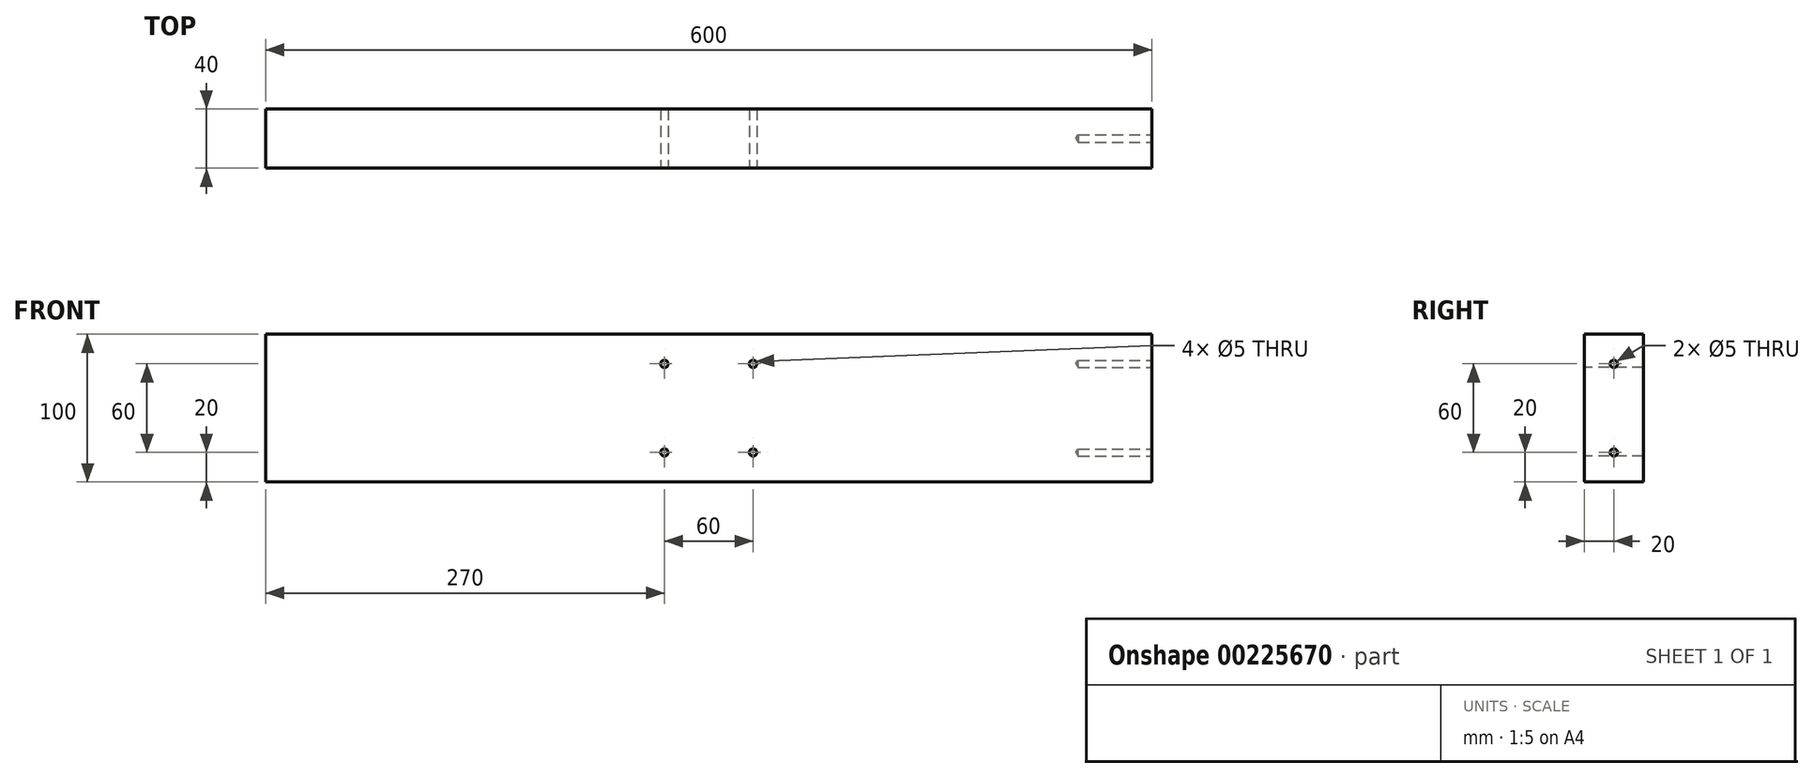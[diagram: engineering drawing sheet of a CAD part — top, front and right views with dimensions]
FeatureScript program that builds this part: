
annotation { "Feature Type Name" : "Feature", "Feature Type Description" : "" }
export const myFeature = defineFeature(function(context is Context, id is Id, definition is map)
    precondition{}
    {
        {
            var Q0;
            Q0=qCreatedBy(makeId("Front.planeOp"),FACE);
            var sketch = newSketch(context, id + "F0", { "sketchPlane" : qUnion([Q0])});
            skLineSegment(sketch, "E0.bottom", {"start": v(-300, 50) * mm, "end": v(300, 50) * mm});
            skLineSegment(sketch, "E0.top", {"start": v(-300, -50) * mm, "end": v(300, -50) * mm});
            skLineSegment(sketch, "E0.left", {"start": v(-300, 50) * mm, "end": v(-300, -50) * mm});
            skLineSegment(sketch, "E0.right", {"start": v(300, 50) * mm, "end": v(300, -50) * mm});
            skLineSegment(sketch, "E1", {"start": v(0, 50) * mm, "end": v(0, -50) * mm, "construction": true});
            skLineSegment(sketch, "E2", {"start": v(-300, 0) * mm, "end": v(300, 0) * mm, "construction": true});
            skSolve(sketch);
        }
        {
            var Q0;
            Q0=makeQuery(id+"F0.imprint","IMPRINT",FACE,{"disambiguationData":[TD([[makeQuery(id+"F0.imprint","IMPRINT",EDGE,{"derivedFrom":sQuery(id+"F0.wireOp",EDGE,"E0.bottom")}),-1.0]])]});
            extrude(context, id + "F1", {"entities" : qUnion([Q0]), "endBound" : BoundingType.SYMMETRIC, "depth" : 40 * mm});
        }
        {
            var Q0;
            Q0=makeQuery(id+"F1.opExtrude","CAP_FACE",FACE,{"disambiguationData":[OSD([sQuery(id+"F0.wireOp",EDGE,"E0.bottom"),sQuery(id+"F0.wireOp",EDGE,"E0.top"),sQuery(id+"F0.wireOp",EDGE,"E0.left"),sQuery(id+"F0.wireOp",EDGE,"E0.right")])],"isStart":false});
            var sketch = newSketch(context, id + "F2", { "sketchPlane" : qUnion([Q0])});
            skLineSegment(sketch, "E3", {"start": v(50, 50) * mm, "end": v(50, -50) * mm, "construction": true});
            skPoint(sketch, "E4", {"position": v(30, 30) * mm});
            skPoint(sketch, "E5", {"position": v(30, -30) * mm});
            skPoint(sketch, "E6", {"position": v(-30, 30) * mm});
            skPoint(sketch, "E7", {"position": v(-30, -30) * mm});
            skSolve(sketch);
        }
        {
            var Q0;
            Q0=sQuery(id+"F2.wireOp",VERTEX,"d4a535e9-99f7-48f2-8113-ce6ab7c4a757");
            var Q1;
            Q1=sQuery(id+"F2.wireOp",VERTEX,"bcf1949b-d54f-4d90-9dce-a7bc10d12a4c");
            var Q2;
            Q2=sQuery(id+"F2.wireOp",VERTEX,"2863efec-cea9-4b0d-8fdf-9ae05410bcc6");
            var Q3;
            Q3=sQuery(id+"F2.wireOp",VERTEX,"1f114518-a88e-412f-a738-b101c2e852a8");
            var Q4;
            Q4=sQuery(id+"F2.wireOp",VERTEX,"E6");
            var Q5;
            Q5=sQuery(id+"F2.wireOp",VERTEX,"E4");
            var Q6;
            Q6=sQuery(id+"F2.wireOp",VERTEX,"E7");
            var Q7;
            Q7=sQuery(id+"F2.wireOp",VERTEX,"E5");
            var Q8;
            Q8=sQuery(id+"F2.wireOp",VERTEX,"6d67d9a1-f94c-460c-9f3e-7900fbfed6ee");
            var Q9;
            Q9=sQuery(id+"F2.wireOp",VERTEX,"3c76ddc9-934c-45bd-b5f3-5c4f99041eee");
            var Q10;
            Q10=sQuery(id+"F2.wireOp",VERTEX,"663380e0-082c-4e9e-85f6-5e861101b0f0");
            var Q11;
            Q11=sQuery(id+"F2.wireOp",VERTEX,"c1c2a8b6-fc07-4b36-872f-67ce65da0087");
            var Q12;
            Q12=makeQuery(id+"F1.opExtrude","SWEPT_BODY",BODY,{"disambiguationData":[OSD([sQuery(id+"F0.wireOp",EDGE,"E0.bottom"),sQuery(id+"F0.wireOp",EDGE,"E0.top"),sQuery(id+"F0.wireOp",EDGE,"E0.left"),sQuery(id+"F0.wireOp",EDGE,"E0.right")])]});
            hole(context, id + "F3", {"style" : HoleStyle.SIMPLE, "endStyle" : HoleEndStyle.THROUGH, "holeDiameter" : 5 * mm, "locations" : qUnion([Q0, Q1, Q2, Q3, Q4, Q5, Q6, Q7, Q8, Q9, Q10, Q11]), "scope" : qUnion([Q12]), "isTappedThrough" : true});
        }
        {
            var Q0;
            Q0=makeQuery(id+"F1.opExtrude","SWEPT_FACE",FACE,{"disambiguationData":[OSD([sQuery(id+"F0.wireOp",EDGE,"E0.right")])]});
            var sketch = newSketch(context, id + "F4", { "sketchPlane" : qUnion([Q0])});
            skPoint(sketch, "E8", {"position": v(0, 30) * mm});
            skPoint(sketch, "E9", {"position": v(0, -30) * mm});
            skSolve(sketch);
        }
        {
            var Q0;
            Q0=sQuery(id+"F4.wireOp",VERTEX,"E8");
            var Q1;
            Q1=sQuery(id+"F4.wireOp",VERTEX,"E9");
            var Q2;
            Q2=makeQuery(id+"F1.opExtrude","SWEPT_BODY",BODY,{"disambiguationData":[OSD([sQuery(id+"F0.wireOp",EDGE,"E0.bottom"),sQuery(id+"F0.wireOp",EDGE,"E0.top"),sQuery(id+"F0.wireOp",EDGE,"E0.left"),sQuery(id+"F0.wireOp",EDGE,"E0.right")])]});
            hole(context, id + "F5", {"style" : HoleStyle.SIMPLE, "endStyle" : HoleEndStyle.BLIND, "holeDiameter" : 5 * mm, "holeDepth" : 50 * mm, "locations" : qUnion([Q0, Q1]), "scope" : qUnion([Q2])});
        }
    });
